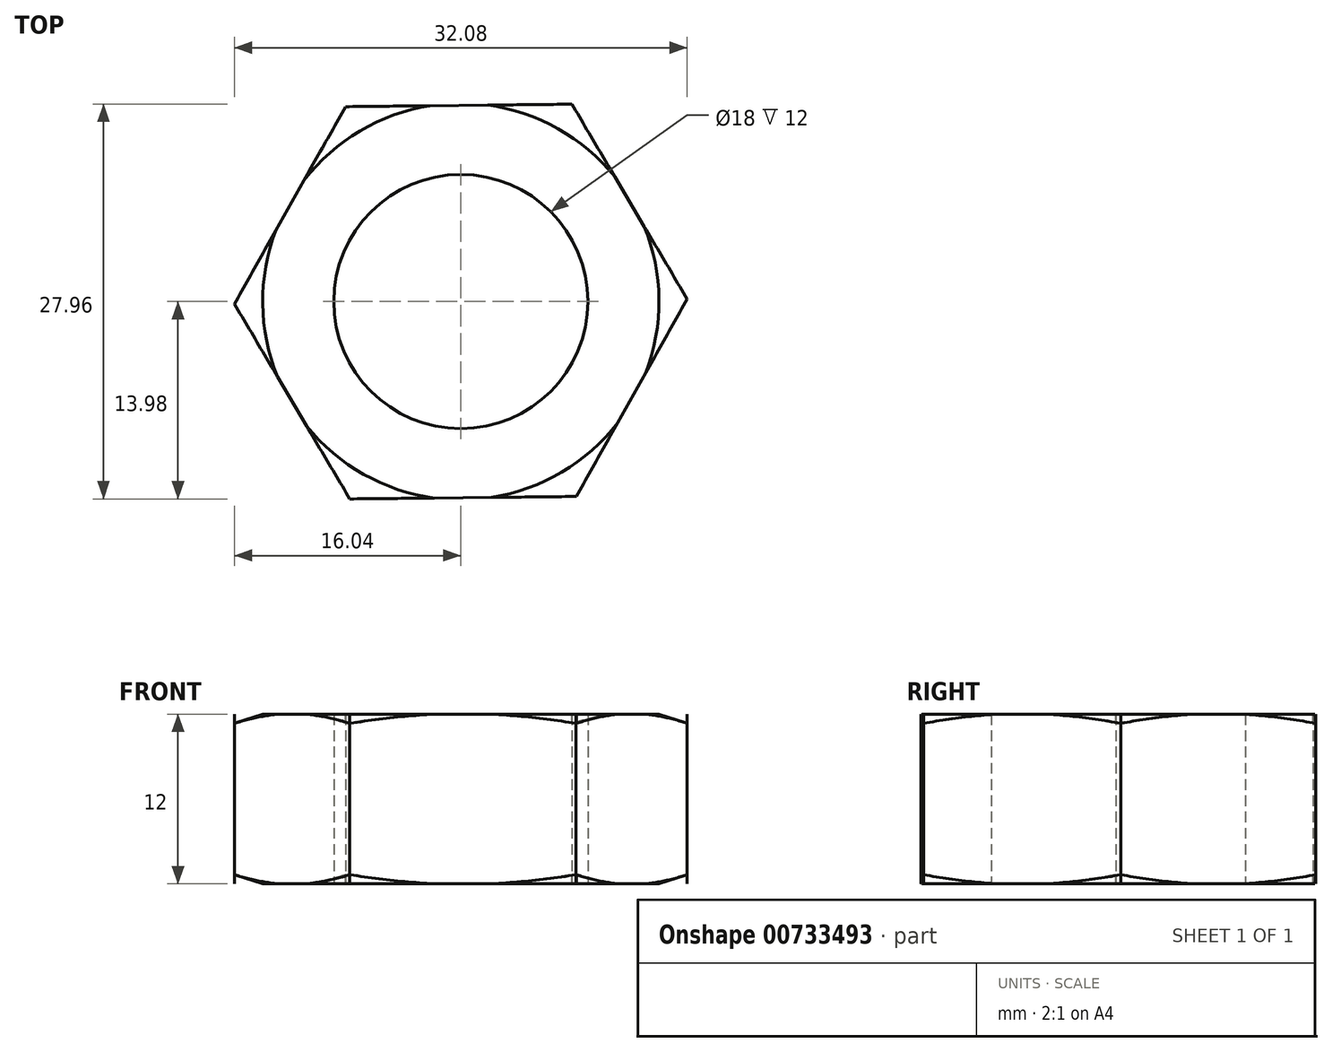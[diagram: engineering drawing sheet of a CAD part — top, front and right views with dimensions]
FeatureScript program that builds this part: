
annotation { "Feature Type Name" : "Feature", "Feature Type Description" : "" }
export const myFeature = defineFeature(function(context is Context, id is Id, definition is map)
    precondition{}
    {
        {
            var Q0;
            Q0=qCreatedBy(makeId("Top.planeOp"),FACE);
            var sketch = newSketch(context, id + "F0", { "sketchPlane" : qUnion([Q0])});
            skCircle(sketch, "E0", {"center": v(0, 0) * mm, "radius": 9 * mm});
            skCircle(sketch, "E1.cCircle", {"center": v(0, 0) * mm, "radius": 13.9 * mm, "construction": true});
            skLineSegment(sketch, "E1.0", {"start": v(-7.87, -13.98) * mm, "end": v(-16.04, -0.17) * mm});
            skLineSegment(sketch, "E1.1", {"start": v(-16.04, -0.17) * mm, "end": v(-8.17, 13.8) * mm});
            skLineSegment(sketch, "E1.2", {"start": v(-8.17, 13.8) * mm, "end": v(7.87, 13.98) * mm});
            skLineSegment(sketch, "E1.3", {"start": v(7.87, 13.98) * mm, "end": v(16.04, 0.17) * mm});
            skLineSegment(sketch, "E1.4", {"start": v(16.04, 0.17) * mm, "end": v(8.17, -13.8) * mm});
            skLineSegment(sketch, "E1.5", {"start": v(8.17, -13.8) * mm, "end": v(-7.87, -13.98) * mm});
            skPoint(sketch, "E1.0.midPoint", {"position": v(-11.96, -7.08) * mm});
            skSolve(sketch);
        }
        {
            var Q0;
            Q0 = qSketchRegion(id + "F0", true);
            extrude(context, id + "F1", {"entities" : qUnion([Q0]), "endBound" : BoundingType.SYMMETRIC, "depth" : 12 * mm, "offsetDistance" : 25 * mm});
        }
        {
            var Q0;
            Q0=qCreatedBy(makeId("Front.planeOp"),FACE);
            var sketch = newSketch(context, id + "F2", { "sketchPlane" : qUnion([Q0])});
            skLineSegment(sketch, "E2.0", {"start": v(-16.04, 6) * mm, "end": v(-16.04, -6) * mm});
            skLineSegment(sketch, "E3", {"start": v(-16.04, 6) * mm, "end": v(-16.04, 5.36) * mm});
            skLineSegment(sketch, "E4", {"start": v(-16.04, 5.36) * mm, "end": v(-14.04, 6) * mm});
            skLineSegment(sketch, "E5", {"start": v(-14.04, 6) * mm, "end": v(-16.04, 6) * mm});
            skLineSegment(sketch, "E6.MirrorCS", {"start": v(-16.04, -6) * mm, "end": v(-16.04, -5.36) * mm});
            skLineSegment(sketch, "E7.MirrorCS", {"start": v(-16.04, -5.36) * mm, "end": v(-14.04, -6) * mm});
            skLineSegment(sketch, "E8.MirrorCS", {"start": v(-14.04, -6) * mm, "end": v(-16.04, -6) * mm});
            skSolve(sketch);
        }
        {
            var Q0;
            Q0 = qSketchRegion(id + "F2", true);
            var Q1;
            Q1=makeQuery(id+"F1.opExtrude","SWEPT_FACE",FACE,{"disambiguationData":[OSD([sQuery(id+"F0.wireOp",EDGE,"E0")])]});
            revolve(context, id + "F3", {"operationType" : NewBodyOperationType.REMOVE, "surfaceOperationType" : NewSurfaceOperationType.NEW, "entities" : qUnion([Q0]), "axis" : qUnion([Q1]), "revolveType" : RevolveType.FULL, "oppositeDirection" : true});
        }
    });
